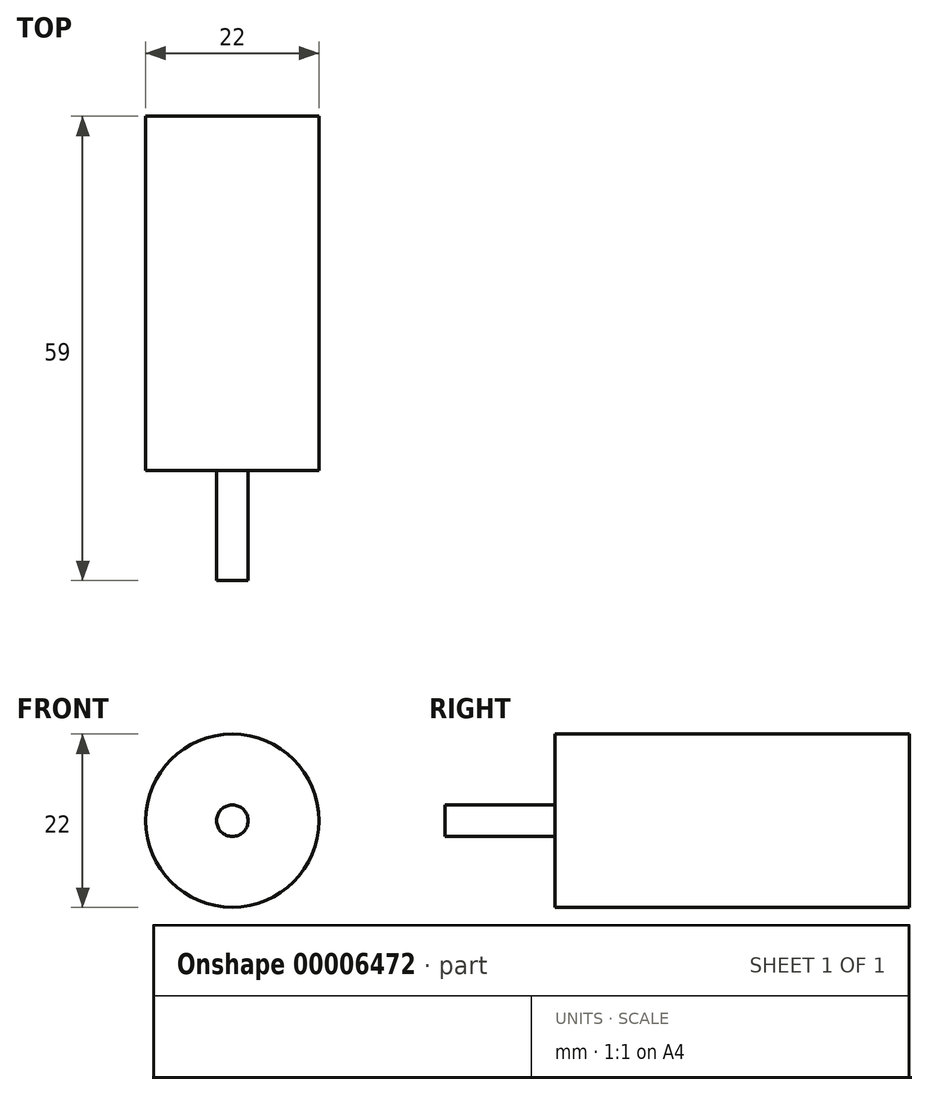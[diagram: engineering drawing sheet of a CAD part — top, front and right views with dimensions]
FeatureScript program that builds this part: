
annotation { "Feature Type Name" : "Feature", "Feature Type Description" : "" }
export const myFeature = defineFeature(function(context is Context, id is Id, definition is map)
    precondition{}
    {
        {
            var Q0;
            Q0=qCreatedBy(makeId("Front.planeOp"),FACE);
            var sketch = newSketch(context, id + "F0", { "sketchPlane" : qUnion([Q0])});
            skCircle(sketch, "E0", {"center": v(0, 0) * mm, "radius": 11 * mm});
            skSolve(sketch);
        }
        {
            var Q0;
            Q0=qSketchRegion(id+"F0",true);
            extrude(context, id + "F1", {"entities" : qUnion([Q0]), "depth" : 29 * mm + 16 * mm});
        }
        {
            var Q0;
            Q0=makeQuery(id+"F1.opExtrude","CAP_FACE",FACE,{"disambiguationData":[OSD([sQuery(id+"F0.wireOp",EDGE,"E0")])],"isStart":false});
            var sketch = newSketch(context, id + "F2", { "sketchPlane" : qUnion([Q0])});
            skCircle(sketch, "E1", {"center": v(0, 0) * mm, "radius": 2 * mm});
            skSolve(sketch);
        }
        {
            var Q0;
            Q0=qSketchRegion(id+"F2",true);
            extrude(context, id + "F3", {"entities" : qUnion([Q0]), "operationType" : NewBodyOperationType.ADD, "depth" : 14 * mm});
        }
    });
